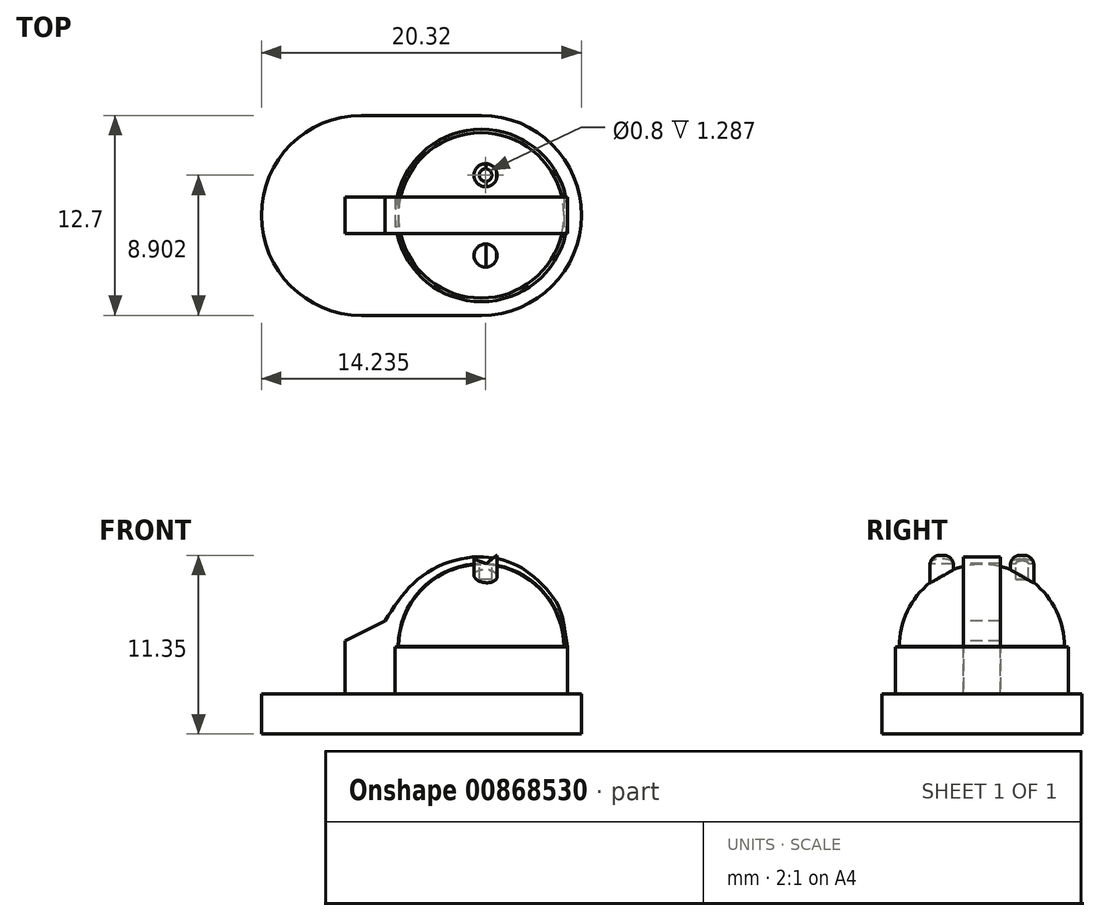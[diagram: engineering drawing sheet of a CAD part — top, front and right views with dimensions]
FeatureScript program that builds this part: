
annotation { "Feature Type Name" : "Feature", "Feature Type Description" : "" }
export const myFeature = defineFeature(function(context is Context, id is Id, definition is map)
    precondition{}
    {
        {
            var Q0;
            Q0=qCreatedBy(makeId("Top.planeOp"),FACE);
            var sketch = newSketch(context, id + "F0", { "sketchPlane" : qUnion([Q0])});
            skLineSegment(sketch, "E0.bottom", {"start": v(-3.81, 6.35) * mm, "end": v(3.8, 6.35) * mm});
            skLineSegment(sketch, "E0.top", {"start": v(-3.81, -6.35) * mm, "end": v(3.8, -6.35) * mm});
            skLineSegment(sketch, "E0.left", {"start": v(-3.81, 6.35) * mm, "end": v(-3.81, -6.35) * mm, "construction": true});
            skLineSegment(sketch, "E0.right", {"start": v(3.8, 6.35) * mm, "end": v(3.81, -6.35) * mm, "construction": true});
            skLineSegment(sketch, "E1", {"start": v(-3.81, 6.35) * mm, "end": v(3.81, -6.35) * mm, "construction": true});
            skLineSegment(sketch, "E2", {"start": v(3.8, 6.35) * mm, "end": v(-3.8, -6.35) * mm, "construction": true});
            skPoint(sketch, "E3", {"position": v(0, 0) * mm});
            skArc(sketch, "E4", {"start": v(-3.81, 6.35) * mm, "mid": v(-10.16, 0) * mm, "end": v(-3.81, -6.35) * mm});
            skArc(sketch, "E5", {"start": v(3.81, 6.35) * mm, "mid": v(10.16, 0) * mm, "end": v(3.81, -6.35) * mm});
            skSolve(sketch);
        }
        {
            var Q0;
            Q0=makeQuery(id+"F0.imprint","IMPRINT",FACE,{"disambiguationData":[TD([[makeQuery(id+"F0.imprint","IMPRINT",EDGE,{"derivedFrom":sQuery(id+"F0.wireOp",EDGE,"E0.bottom")}),-1.0]])]});
            extrude(context, id + "F1", {"entities" : qUnion([Q0]), "depth" : 2.54 * mm, "offsetDistance" : 25.4 * mm});
        }
        {
            var Q0;
            Q0=makeQuery(id+"F1.opExtrude","CAP_FACE",FACE,{"disambiguationData":[OSD([sQuery(id+"F0.wireOp",EDGE,"E0.bottom"),sQuery(id+"F0.wireOp",EDGE,"E0.top"),sQuery(id+"F0.wireOp",EDGE,"E4"),sQuery(id+"F0.wireOp",EDGE,"E5")])],"isStart":false});
            var sketch = newSketch(context, id + "F2", { "sketchPlane" : qUnion([Q0])});
            skCircle(sketch, "E6", {"center": v(3.8, 0) * mm, "radius": 5.48 * mm});
            skSolve(sketch);
        }
        {
            var Q0;
            Q0 = qSketchRegion(id + "F2", true);
            extrude(context, id + "F3", {"entities" : qUnion([Q0]), "depth" : 3 * mm, "offsetDistance" : 25.4 * mm});
        }
        {
            var Q0;
            Q0=qCreatedBy(makeId("Front.planeOp"),FACE);
            var sketch = newSketch(context, id + "F4", { "sketchPlane" : qUnion([Q0])});
            skArc(sketch, "E7", {"start": v(3.8, 10.78) * mm, "mid": v(0.1, 9.25) * mm, "end": v(-1.46, 5.56) * mm});
            skLineSegment(sketch, "E8", {"start": v(3.8, 10.78) * mm, "end": v(3.8, 5.53) * mm});
            skLineSegment(sketch, "E9", {"start": v(-1.46, 5.56) * mm, "end": v(3.8, 5.53) * mm});
            skSolve(sketch);
        }
        {
            var Q0;
            Q0=makeQuery(id+"F4.imprint","IMPRINT",FACE,{"disambiguationData":[TD([[makeQuery(id+"F4.imprint","IMPRINT",EDGE,{"derivedFrom":sQuery(id+"F4.wireOp",EDGE,"E7")}),1.0]])]});
            var Q1;
            Q1=sQuery(id+"F4.wireOp",EDGE,"E8");
            revolve(context, id + "F5", {"surfaceOperationType" : NewSurfaceOperationType.NEW, "entities" : qUnion([Q0]), "axis" : qUnion([Q1]), "revolveType" : RevolveType.FULL});
        }
        {
            var Q0;
            Q0=qCreatedBy(makeId("Front.planeOp"),FACE);
            var sketch = newSketch(context, id + "F6", { "sketchPlane" : qUnion([Q0])});
            skPoint(sketch, "E10", {"position": v(-1.67, 2.56) * mm});
            skPoint(sketch, "E11", {"position": v(-4.85, 2.59) * mm});
            skPoint(sketch, "E12", {"position": v(-4.85, 5.91) * mm});
            skPoint(sketch, "E13", {"position": v(-2.3, 7.18) * mm});
            skLineSegment(sketch, "E14", {"start": v(-1.67, 2.56) * mm, "end": v(-4.85, 2.59) * mm});
            skLineSegment(sketch, "E15", {"start": v(-4.85, 5.91) * mm, "end": v(-2.3, 7.18) * mm});
            skLineSegment(sketch, "E16", {"start": v(-4.85, 5.91) * mm, "end": v(-4.85, 2.59) * mm});
            skPoint(sketch, "E17", {"position": v(9.29, 5.56) * mm});
            skFitSpline(sketch, "E18", {"points": [v(-2.3, 7.18) * mm, v(0, 10.01) * mm, v(3.47, 11.26) * mm, v(5.8, 10.84) * mm, v(7.07, 10.05) * mm, v(8.38, 8.66) * mm, v(8.9, 7.6) * mm, v(9.29, 5.56) * mm], "startDerivative": vector(10.84, 17.2) * mm, "endDerivative": vector(2.5, -16.26) * mm});
            skPoint(sketch, "E19", {"position": v(-1.66, 5.55) * mm});
            skPoint(sketch, "E20", {"position": v(-1.47, 5.57) * mm});
            skPoint(sketch, "E21", {"position": v(9.05, 5.56) * mm});
            skLineSegment(sketch, "E22", {"start": v(-1.67, 2.56) * mm, "end": v(-1.66, 5.55) * mm});
            skArc(sketch, "E23", {"start": v(-1.47, 5.57) * mm, "mid": v(3.8, 10.83) * mm, "end": v(9.05, 5.56) * mm});
            skLineSegment(sketch, "E24", {"start": v(9.05, 5.56) * mm, "end": v(9.29, 5.56) * mm});
            skLineSegment(sketch, "E25", {"start": v(-1.66, 5.55) * mm, "end": v(-1.47, 5.55) * mm});
            skLineSegment(sketch, "E26", {"start": v(-1.47, 5.55) * mm, "end": v(-1.47, 5.57) * mm});
            skSolve(sketch);
        }
        {
            var Q0;
            Q0=makeQuery(id+"F6.imprint","IMPRINT",FACE,{"disambiguationData":[TD([[makeQuery(id+"F6.imprint","IMPRINT",EDGE,{"derivedFrom":sQuery(id+"F6.wireOp",EDGE,"E14")}),-1.0]])]});
            extrude(context, id + "F7", {"entities" : qUnion([Q0]), "oppositeDirection" : true, "depth" : 2.34 * mm, "offsetDistance" : 25.4 * mm, "symmetric" : true});
        }
        {
            var Q0;
            Q0=makeQuery(id+"F1.opExtrude","CAP_FACE",FACE,{"disambiguationData":[OSD([sQuery(id+"F0.wireOp",EDGE,"E0.bottom"),sQuery(id+"F0.wireOp",EDGE,"E0.top"),sQuery(id+"F0.wireOp",EDGE,"E4"),sQuery(id+"F0.wireOp",EDGE,"E5")])],"isStart":false});
            cPlane(context, id + "F8", {"entities" : qUnion([Q0]), "cplaneType" : CPlaneType.OFFSET, "offset" : 7.04 * mm, "width" : 152.4 * mm, "height" : 152.4 * mm});
        }
        {
            var Q0;
            Q0=qCreatedBy(id+"F8.planeOp",FACE);
            var sketch = newSketch(context, id + "F9", { "sketchPlane" : qUnion([Q0])});
            skLineSegment(sketch, "E27", {"start": v(0, 0) * mm, "end": v(10.19, 0) * mm});
            skCircle(sketch, "E28", {"center": v(4.07, 2.55) * mm, "radius": 0.74 * mm});
            skCircle(sketch, "E29.MirrorC", {"center": v(4.07, -2.55) * mm, "radius": 0.74 * mm});
            skSolve(sketch);
        }
        {
            var Q0;
            Q0 = qSketchRegion(id + "F9", true);
            extrude(context, id + "F10", {"entities" : qUnion([Q0]), "operationType" : NewBodyOperationType.ADD, "depth" : 1.78 * mm, "offsetDistance" : 25.4 * mm});
        }
        {
            var Q0;
            Q0=makeQuery(id+"F10.opExtrude","CAP_FACE",FACE,{"disambiguationData":[OSD([sQuery(id+"F9.wireOp",EDGE,"E28")])],"isStart":false});
            var sketch = newSketch(context, id + "F11", { "sketchPlane" : qUnion([Q0])});
            skCircle(sketch, "E30", {"center": v(4.07, 2.55) * mm, "radius": 0.4 * mm});
            skCircle(sketch, "E31.MirrorC", {"center": v(4.07, -2.55) * mm, "radius": 0.4 * mm});
            skSolve(sketch);
        }
        {
            var Q0;
            Q0=makeQuery(id+"F11.imprint","IMPRINT",FACE,{"disambiguationData":[TD([[makeQuery(id+"F11.imprint","IMPRINT",EDGE,{"derivedFrom":sQuery(id+"F11.wireOp",EDGE,"E31.MirrorC")}),-1.0]])]});
            var Q1;
            Q1=makeQuery(id+"F11.imprint","IMPRINT",FACE,{"disambiguationData":[TD([[makeQuery(id+"F11.imprint","IMPRINT",EDGE,{"derivedFrom":sQuery(id+"F11.wireOp",EDGE,"E30")}),1.0]])]});
            extrude(context, id + "F12", {"entities" : qUnion([Q0, Q1]), "operationType" : NewBodyOperationType.REMOVE, "oppositeDirection" : true, "depth" : 1.52 * mm, "offsetDistance" : 25.4 * mm});
        }
        {
            var Q0;
            Q0=qCreatedBy(makeId("Front.planeOp"),FACE);
            cPlane(context, id + "F13", {"entities" : qUnion([Q0]), "cplaneType" : CPlaneType.OFFSET, "offset" : 2.54 * mm, "width" : 152.4 * mm, "height" : 152.4 * mm});
        }
        {
            var Q0;
            Q0=qCreatedBy(id+"F13.planeOp",FACE);
            var sketch = newSketch(context, id + "F14", { "sketchPlane" : qUnion([Q0])});
            skLineSegment(sketch, "E32", {"start": v(4.78, 11.37) * mm, "end": v(4.11, 10.82) * mm});
            skLineSegment(sketch, "E33", {"start": v(4.11, 10.82) * mm, "end": v(3.32, 11.13) * mm});
            skLineSegment(sketch, "E34", {"start": v(3.32, 11.13) * mm, "end": v(3.32, 11.4) * mm});
            skLineSegment(sketch, "E35", {"start": v(3.32, 11.4) * mm, "end": v(4.78, 11.37) * mm});
            skSolve(sketch);
        }
        {
            var Q0;
            Q0 = qSketchRegion(id + "F14", true);
            extrude(context, id + "F15", {"entities" : qUnion([Q0]), "oppositeDirection" : true, "depth" : 14.17 * mm, "offsetDistance" : 25.4 * mm, "symmetric" : true});
        }
        {
            var Q0;
            Q0=makeQuery(id+"F15.opExtrude","SWEPT_BODY",BODY,{"disambiguationData":[OSD([sQuery(id+"F14.wireOp",EDGE,"E32"),sQuery(id+"F14.wireOp",EDGE,"E33"),sQuery(id+"F14.wireOp",EDGE,"E34"),sQuery(id+"F14.wireOp",EDGE,"E35")])]});
            var Q1;
            Q1=makeQuery(id+"F5.opRevolve","SWEPT_BODY",BODY,{"disambiguationData":[OSD([sQuery(id+"F4.wireOp",EDGE,"E7"),sQuery(id+"F4.wireOp",EDGE,"E8"),sQuery(id+"F4.wireOp",EDGE,"E9")])]});
            booleanBodies(context, id + "F16", {"operationType" : BooleanOperationType.SUBTRACTION, "tools" : qUnion([Q0]), "targets" : qUnion([Q1])});
        }
    });
